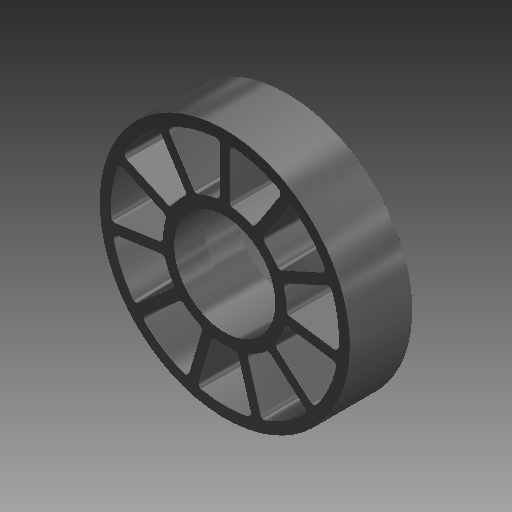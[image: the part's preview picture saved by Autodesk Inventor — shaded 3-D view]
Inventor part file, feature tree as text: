
AUTODESK INVENTOR PART (.ipt)
format: ipt  version: 2019 (Build 230136000, 136)  size: 873,472 bytes
history: native  units: mm (DEFAULTED — no unit token found)
features: fillet x1
ambient origin geometry x8: Origin, YZ Plane, XZ Plane, XY Plane, X Axis, Y Axis, Z Axis, Center Point
bodies: Solid1 (feature_tree)
feature tree (1):
  fillet  "Fillet2"  [1 undecoded]
note: 1 required parameter value undecoded (feature->parameter linkage not recoverable at this tier; creation-order binding heuristic only, values carry confidence <= 0.55)
